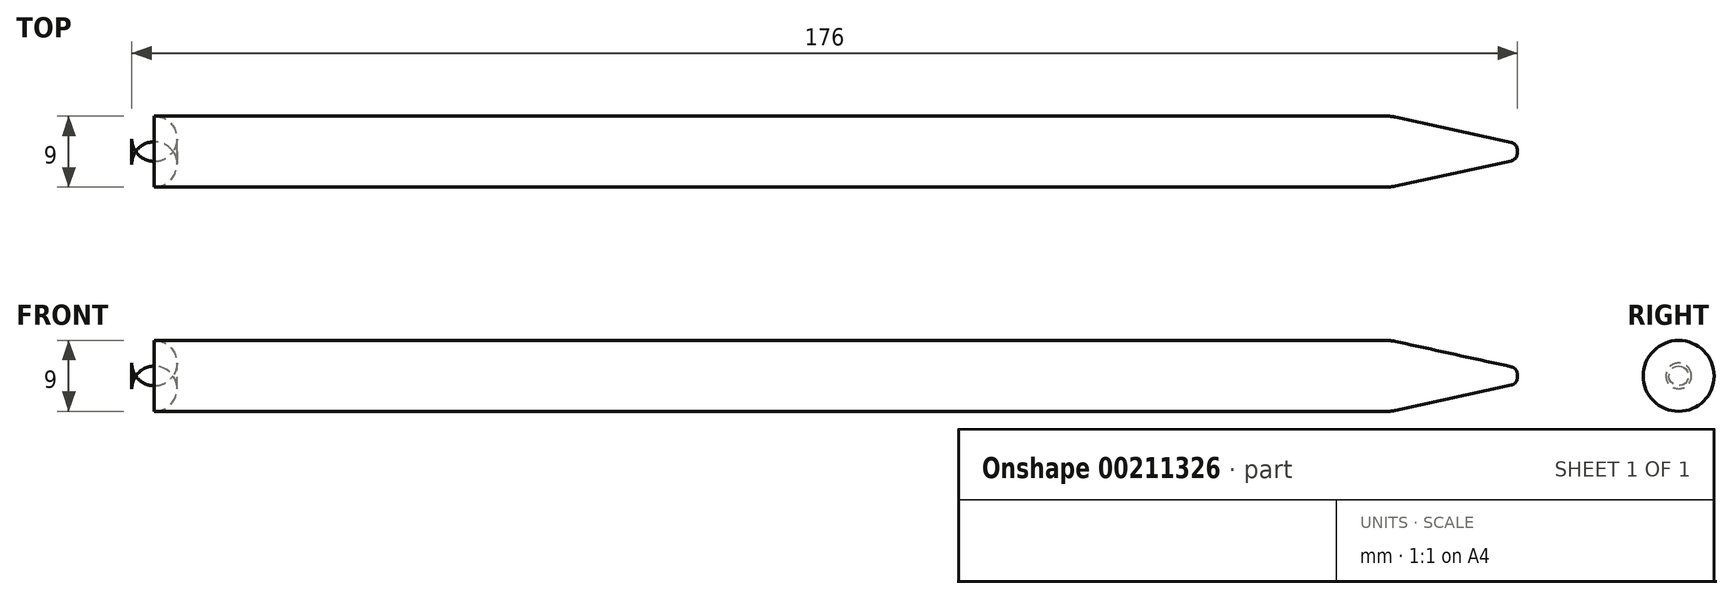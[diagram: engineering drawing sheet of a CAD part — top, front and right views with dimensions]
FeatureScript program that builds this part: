
annotation { "Feature Type Name" : "Feature", "Feature Type Description" : "" }
export const myFeature = defineFeature(function(context is Context, id is Id, definition is map)
    precondition{}
    {
        {
            var Q0;
            Q0=qCreatedBy(makeId("Top.planeOp"),FACE);
            var sketch = newSketch(context, id + "F0", { "sketchPlane" : qUnion([Q0])});
            skLineSegment(sketch, "E0", {"start": v(-38.18, 0) * mm, "end": v(38.2, 0) * mm, "construction": true});
            skLineSegment(sketch, "E1", {"start": v(-34.7, 4.5) * mm, "end": v(125.3, 4.5) * mm});
            skLineSegment(sketch, "E2", {"start": v(141.3, 1) * mm, "end": v(125.3, 4.5) * mm});
            skLineSegment(sketch, "E3", {"start": v(141.3, 1) * mm, "end": v(141.3, 0) * mm});
            skLineSegment(sketch, "E4", {"start": v(141.3, 0) * mm, "end": v(-34.7, 0) * mm});
            skLineSegment(sketch, "E5", {"start": v(-34.7, 4.5) * mm, "end": v(-34.7, 0) * mm});
            skSolve(sketch);
        }
        {
            var Q0;
            Q0=makeQuery(id+"F0.imprint","IMPRINT",FACE,{"disambiguationData":[TD([[makeQuery(id+"F0.imprint","IMPRINT",EDGE,{"derivedFrom":sQuery(id+"F0.wireOp",EDGE,"E1")}),-1.0]])]});
            var Q1;
            Q1=sQuery(id+"F0.wireOp",EDGE,"E0");
            revolve(context, id + "F1", {"entities" : qUnion([Q0]), "axis" : qUnion([Q1]), "revolveType" : RevolveType.FULL});
        }
        {
            var Q0;
            Q0=makeQuery(id+"F1.opRevolve","SWEPT_EDGE",EDGE,{"disambiguationData":[OSD([sQuery(id+"F0.wireOp",EDGE,"E1"),sQuery(id+"F0.wireOp",EDGE,"E5")])]});
            fillet(context, id + "F2", {"entities" : qUnion([Q0]), "radius" : 2.87 * mm, "tangentPropagation" : true, "allowEdgeOverflow" : false});
        }
        {
            var Q0;
            Q0=makeQuery(id+"F1.opRevolve","SWEPT_EDGE",EDGE,{"disambiguationData":[OSD([sQuery(id+"F0.wireOp",EDGE,"E2"),sQuery(id+"F0.wireOp",EDGE,"E3")])]});
            fillet(context, id + "F3", {"entities" : qUnion([Q0]), "radius" : 0.97 * mm, "tangentPropagation" : true, "allowEdgeOverflow" : false});
        }
        {
            var Q0;
            Q0=makeQuery(id+"F1.opRevolve","SWEPT_EDGE",EDGE,{"disambiguationData":[OSD([sQuery(id+"F0.wireOp",EDGE,"E1"),sQuery(id+"F0.wireOp",EDGE,"E2")])]});
            fillet(context, id + "F4", {"entities" : qUnion([Q0]), "radius" : 5.08 * mm, "tangentPropagation" : true, "allowEdgeOverflow" : false});
        }
    });
